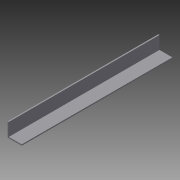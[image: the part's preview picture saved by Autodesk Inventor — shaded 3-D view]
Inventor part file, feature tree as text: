
AUTODESK INVENTOR PART (.ipt)
format: ipt  version: 2015 (Build 190159000, 159)  size: 93,184 bytes
history: native  units: in
note: dims shown in document units (in); Inventor stores cm internally (conversion verified against a paired STEP export)
features: extrude x3, sketch x3
ambient origin geometry x8: Origin, YZ Plane, XZ Plane, XY Plane, X Axis, Y Axis, Z Axis, Center Point
bodies: Solid1 (feature_tree)
feature tree (6):
  extrude  "Extrusion1"  Depth=0.125in
  extrude  "Extrusion2"  Depth=0.125in
  extrude  "Extrusion3"  Depth=1.5in TaperAngle=0.0deg
  sketch  "Sketch1"  dims[d0=1.5in d1=0.125in]
  sketch  "Sketch2"  dims[d2=14.0in d3=0.0in d4=0.125in]
  sketch  "Sketch3"  dims[d5=1.5in d6=14.0in d7=0.0in d8=2.0in d9=0.0in]
